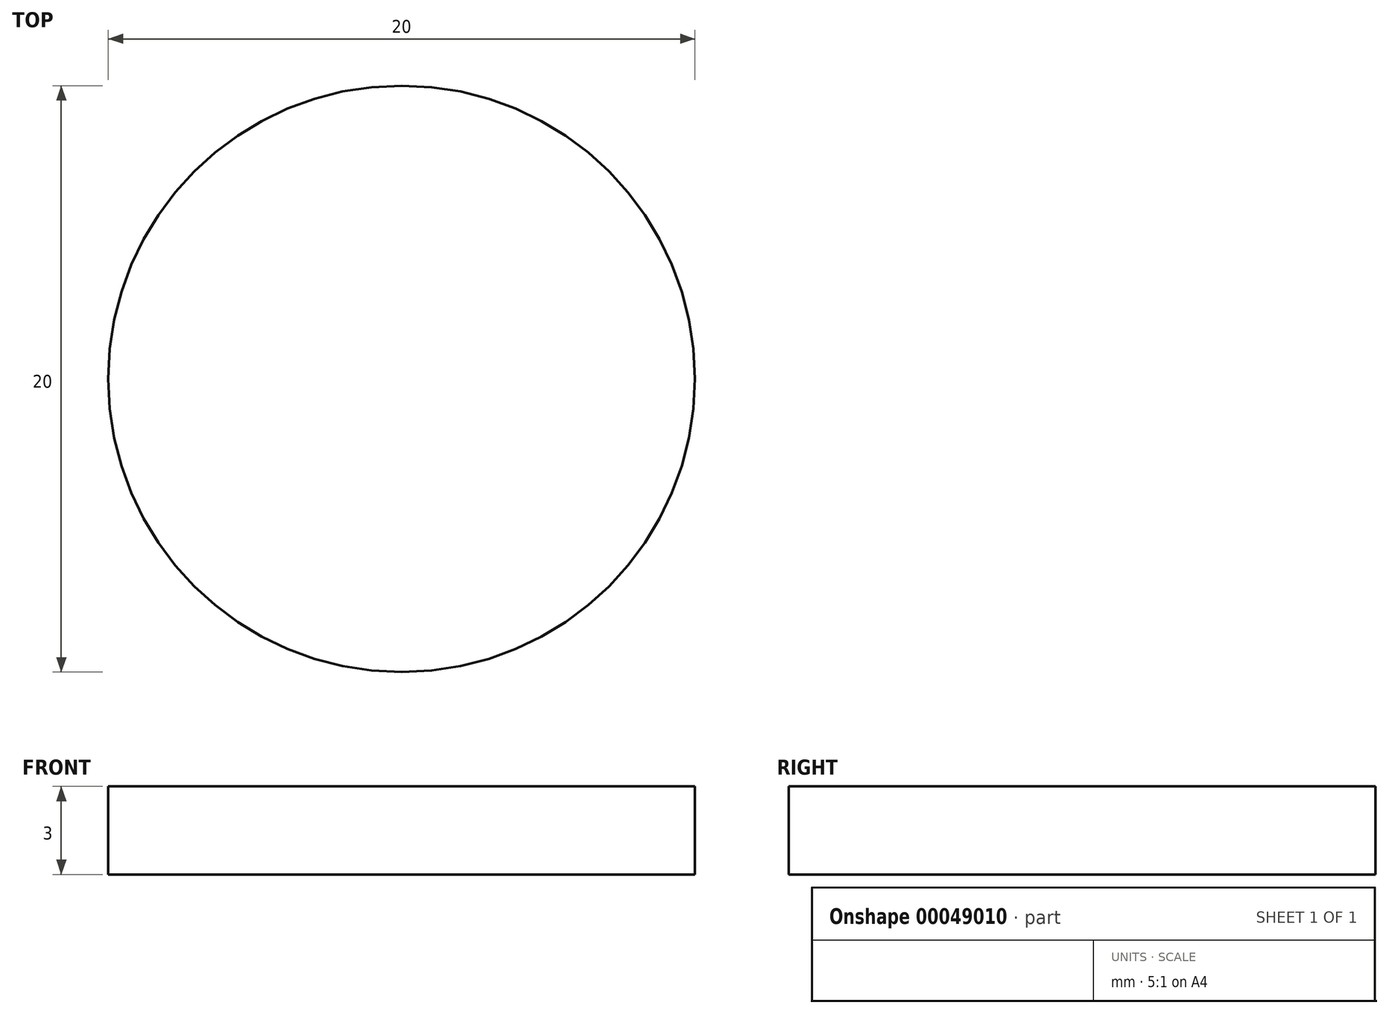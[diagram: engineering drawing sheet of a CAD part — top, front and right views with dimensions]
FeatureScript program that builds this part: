
annotation { "Feature Type Name" : "Feature", "Feature Type Description" : "" }
export const myFeature = defineFeature(function(context is Context, id is Id, definition is map)
    precondition{}
    {
        {
            var Q0;
            Q0=qCreatedBy(makeId("Top.planeOp"),FACE);
            var sketch = newSketch(context, id + "F0", { "sketchPlane" : qUnion([Q0])});
            skCircle(sketch, "E0", {"center": v(0, 0) * mm, "radius": 10 * mm});
            skSolve(sketch);
        }
        {
            var Q0;
            Q0=sQuery(id+"F0.wireOp",EDGE,"E0");
            extrude(context, id + "F1", {"bodyType" : ToolBodyType.SURFACE, "surfaceEntities" : qUnion([Q0]), "depth" : 3 * mm});
        }
    });
